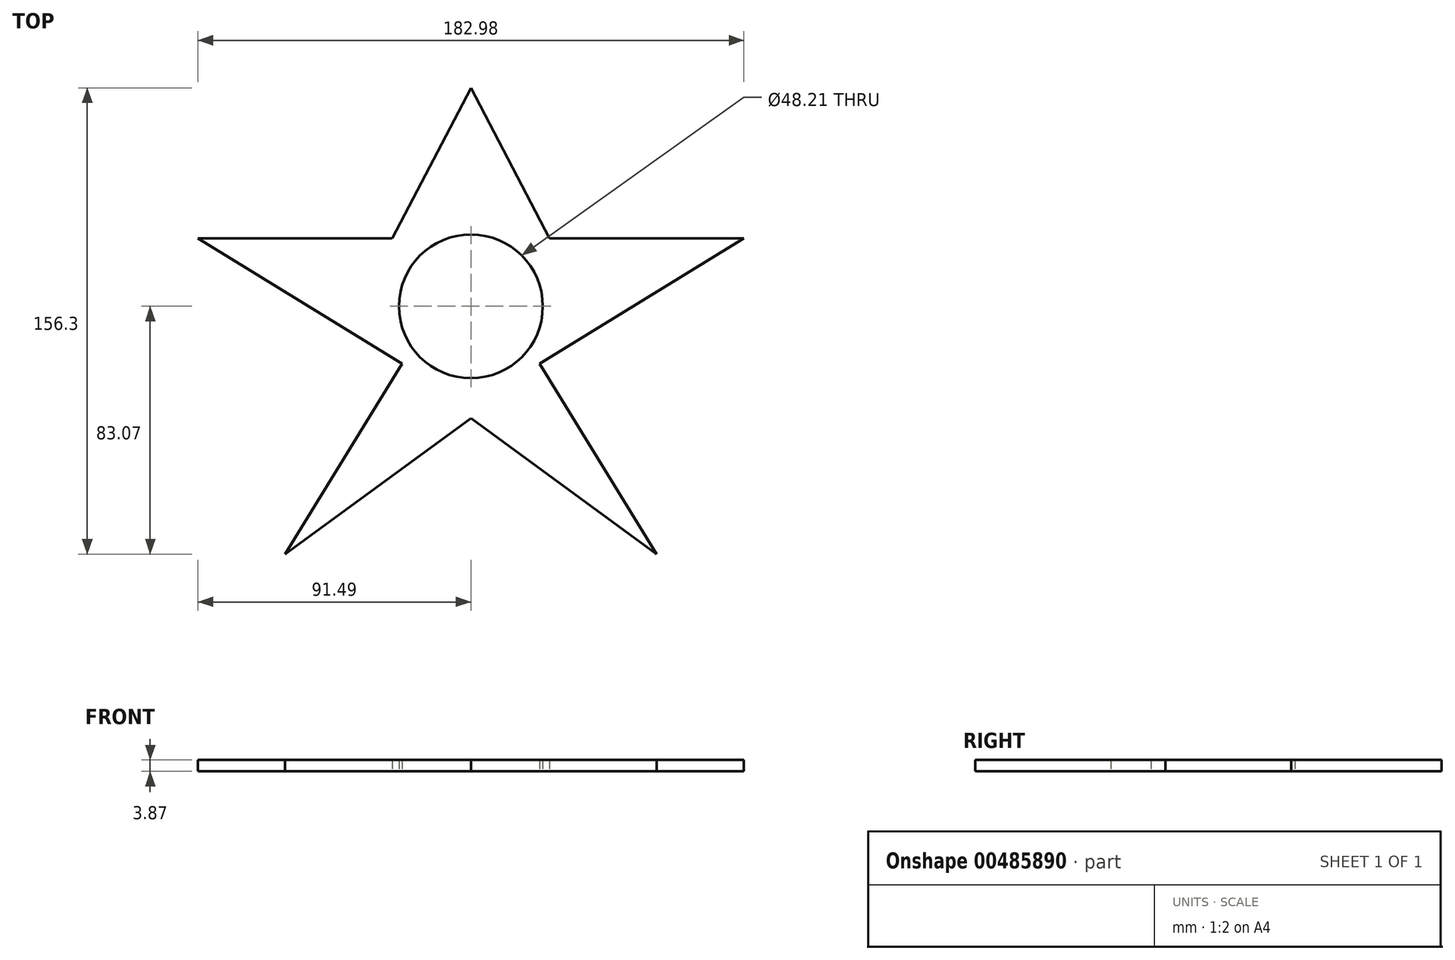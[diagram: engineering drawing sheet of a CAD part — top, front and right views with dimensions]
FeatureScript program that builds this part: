
annotation { "Feature Type Name" : "Feature", "Feature Type Description" : "" }
export const myFeature = defineFeature(function(context is Context, id is Id, definition is map)
    precondition{}
    {
        {
            var Q0;
            Q0=qCreatedBy(makeId("Top.planeOp"),FACE);
            var sketch = newSketch(context, id + "F0", { "sketchPlane" : qUnion([Q0])});
            skLineSegment(sketch, "E0", {"start": v(-26.35, 22.82) * mm, "end": v(-91.49, 22.82) * mm});
            skLineSegment(sketch, "E1", {"start": v(-91.49, 22.82) * mm, "end": v(-23.03, -19.3) * mm});
            skLineSegment(sketch, "E2", {"start": v(-23.03, -19.3) * mm, "end": v(-62.26, -83.07) * mm});
            skLineSegment(sketch, "E3", {"start": v(-62.26, -83.07) * mm, "end": v(0, -37.55) * mm});
            skPoint(sketch, "E4.start.orphan", {"position": v(0, 83.2) * mm});
            skLineSegment(sketch, "E5", {"start": v(-26.35, 22.82) * mm, "end": v(0, 73.23) * mm});
            skLineSegment(sketch, "E6.MirrorCS", {"start": v(26.35, 22.82) * mm, "end": v(0, 73.23) * mm});
            skLineSegment(sketch, "E7.MirrorCS", {"start": v(26.35, 22.82) * mm, "end": v(91.49, 22.82) * mm});
            skLineSegment(sketch, "E8.MirrorCS", {"start": v(91.49, 22.82) * mm, "end": v(23.03, -19.3) * mm});
            skLineSegment(sketch, "E9.MirrorCS", {"start": v(23.03, -19.3) * mm, "end": v(62.26, -83.07) * mm});
            skLineSegment(sketch, "E10.MirrorCS", {"start": v(62.26, -83.07) * mm, "end": v(0, -37.55) * mm});
            skPoint(sketch, "E11.start.orphan", {"position": v(0, -63.33) * mm});
            skCircle(sketch, "E12", {"center": v(0, 0) * mm, "radius": 24.1 * mm});
            skSolve(sketch);
        }
        {
            var Q0;
            Q0=makeQuery(id+"F0.imprint","IMPRINT",FACE,{"disambiguationData":[TD([[makeQuery(id+"F0.imprint","IMPRINT",EDGE,{"derivedFrom":sQuery(id+"F0.wireOp",EDGE,"E0")}),1.0]])]});
            extrude(context, id + "F1", {"entities" : qUnion([Q0]), "depth" : 3.87 * mm});
        }
    });
